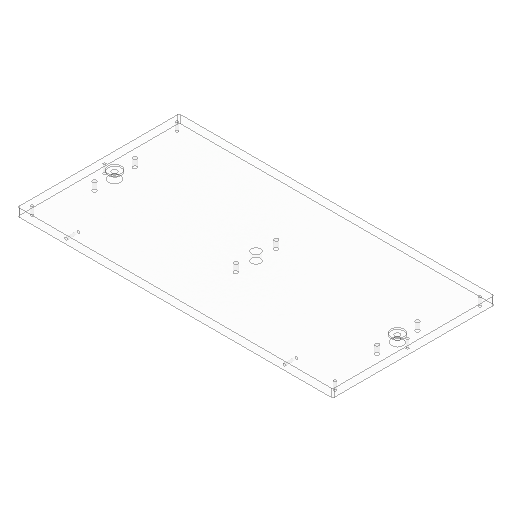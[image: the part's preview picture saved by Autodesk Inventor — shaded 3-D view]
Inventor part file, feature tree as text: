
AUTODESK INVENTOR PART (.ipt)
format: ipt  version: 2025.2 (Build 292293000, 293)  size: 241,152 bytes
history: native  units: in
note: dims shown in document units (in); Inventor stores cm internally (conversion verified against a paired STEP export)
features: hole x7, sketch x6, extrude x1, fillet x1
ambient origin geometry x8: Origin, YZ Plane, XZ Plane, XY Plane, X Axis, Y Axis, Z Axis, Center Point
bodies: Solid1 (feature_tree)
feature tree (15):
  extrude  "Extrusion1"  Depth=7.874in
  sketch  "Sketch2"  dims[d5=13.7795in d6=14.203in]
  hole  "Hole1"  [1 undecoded]
  hole  "Hole2"  [1 undecoded]
  hole  "Hole3"  [1 undecoded]
  hole  "Hole4"  [1 undecoded]
  sketch  "Sketch4"  dims[d15=0.4724in]
  hole  "Hole5"  [1 undecoded]
  hole  "Hole6"  [1 undecoded]
  hole  "Hole10"  [1 undecoded]
  fillet  "Fillet1"  Radius=0.3937in
  sketch  "Sketch1"  dims[d0=15.3543in d1=7.874in]
  sketch  "Sketch3"  dims[d7=0.1936in d8=0.4724in d9=0.1575in d10=0.0787in d11=90.0deg d12=0.315in d13=0.8108in d14=13.7795in]
  sketch  "Sketch Rectangular Pattern1"  dims[d2=0.3937in d3=0.0in d4=0.0787in]
  sketch  "Sketch10"  dims[d16=0.2559in d17=0.4724in d18=0.6496in d19=0.0787in d20=90.0deg d21=0.315in d22=0.8108in d25=0.3937in d26=14.1732in d27=7.0866in d28=0.3937in d29=0.3937in d30=0.7874in d31=7.0866in d33=0.7874in d34=3.5433in d36=0.7874in d39=0.5906in d40=0.1936in d41=0.4724in d42=0.7874in d43=0.0787in d44=90.0deg d45=0.315in d46=0.8108in d47=0.4331in d48=0.4724in d49=0.119in d50=0.0787in d51=0.5635in d52=0.0787in d53=0.0in d54=13.9194in d55=0.2559in d56=0.2362in d57=0.5709in d58=0.2677in d59=90.0deg d60=0.315in d61=0.8108in d62=7.0866in d63=0.2953in d64=0.1276in d65=0.315in d66=0.315in d67=0.1811in d68=90.0deg d69=0.315in d70=0.8108in d95=10.6299in d96=0.1276in d97=0.4724in d98=0.6496in d99=0.0787in d100=90.0deg d101=0.5906in d102=0.8108in d103=0.2362in d104=13.7795in d105=1.9685in d71=0.0394in d72=0.0394in d73=0.0394in d74=0.0059in d75=0.0098in d76=0.0148in d77=0.5635in d78=0.0295in d79=0.8108in d80=0.0025in d81=0.0295in d82=0.0148in]
note: 7 required parameter values undecoded (feature->parameter linkage not recoverable at this tier; creation-order binding heuristic only, values carry confidence <= 0.55)
